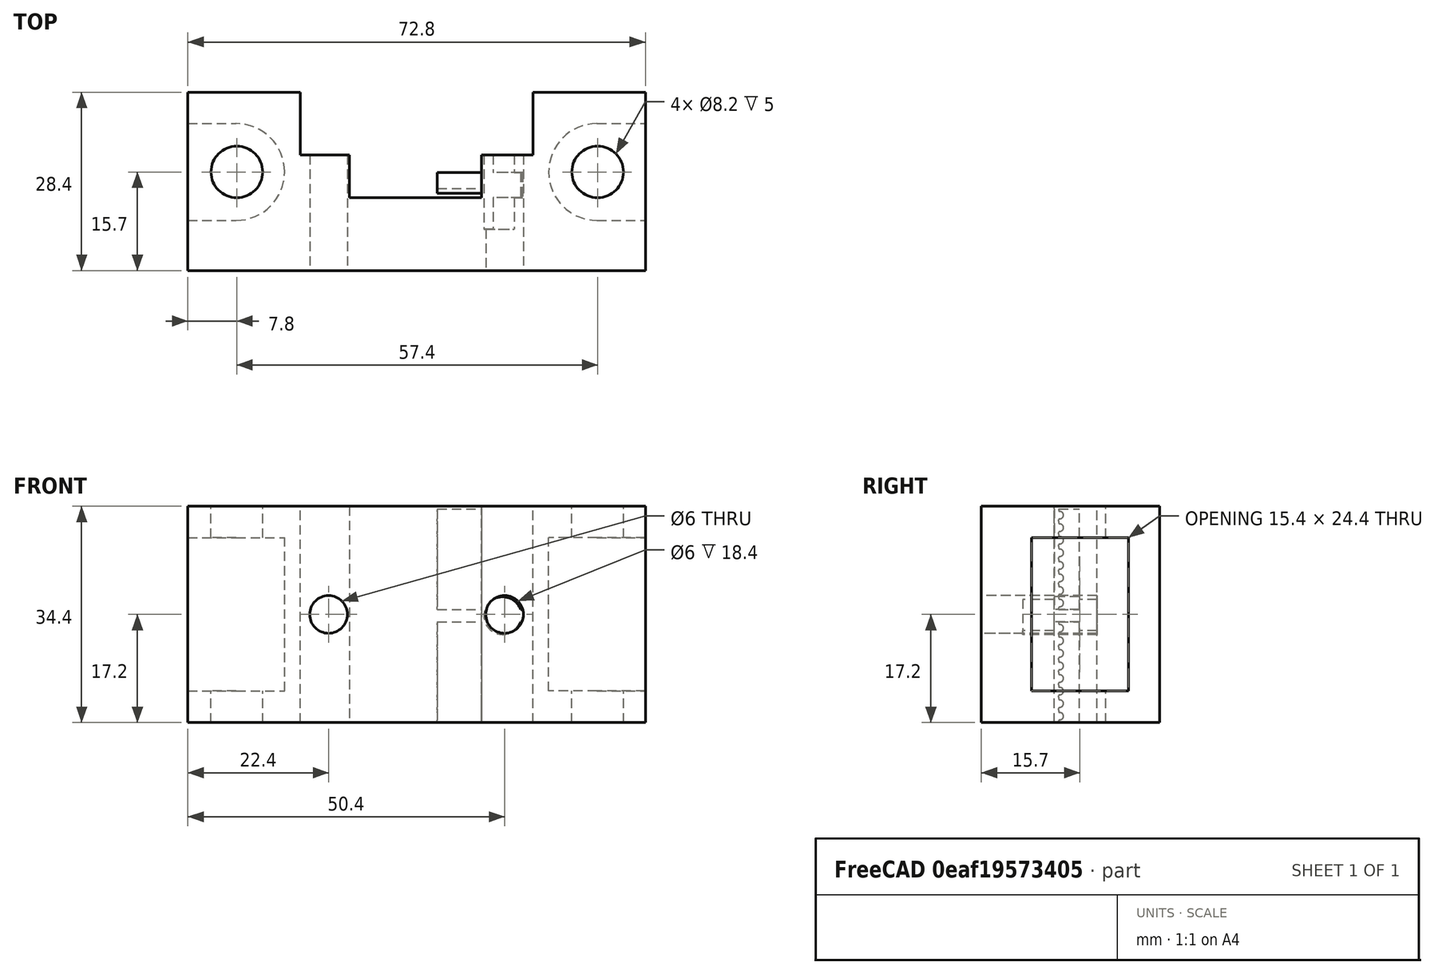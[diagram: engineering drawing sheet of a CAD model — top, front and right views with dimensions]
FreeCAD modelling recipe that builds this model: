
FCSTD DOCUMENT  (FreeCAD 0.18R16110 (Git))
Label: z-slide
License: All rights reserved
LicenseURL: http://en.wikipedia.org/wiki/All_rights_reserved
objects: Part::Cut×12, Part::Box×8, Part::Extrusion×8, Part::Cylinder×7, Part::MultiFuse×5, Spreadsheet::Sheet×2, Sketcher::SketchObject×1, Mesh::Feature×1
note: 41 computed .brp shape members not serialized (recipe doc carries the construction recipe); baked Part::Feature solids carry a one-line shape summary decoded from their .brp

FEATURE [Part::Box] Box017  label="Quader011"
  AttacherType = Attacher::AttachEngine3D
  Height = 34.4
  Length = 72.8
  Placement = pos=(1.3,-28.6,-15) rot=(0,0,1;0rad)
  Width = 3
  expr: Placement.Base.y = -Spreadsheet.z_bs - Spreadsheet.tolerance - 3
  expr: Placement.Base.x = (Spreadsheet.z_lmount - Spreadsheet.z_ls) / 2
  expr: Height = Spreadsheet.z_hs
  expr: Length = Spreadsheet.z_ls
FEATURE [Part::Cylinder] Cylinder038  label="Zylinder030"
  Angle = 360
  AttacherType = Attacher::AttachEngine3D
  Height = 25
  Placement = pos=(51.7,-5,2.2) rot=(1,0,0;1.5708rad)
  Radius = 3
  expr: Placement.Base.x = (Spreadsheet.z_lmount - Spreadsheet.z_ls) / 2 + Spreadsheet.z_ls / 2 + 14
  expr: Placement.Base.z = -15 + Spreadsheet.z_hs / 2
FEATURE [Part::Cylinder] Cylinder037  label="Zylinder029"
  Angle = 360
  AttacherType = Attacher::AttachEngine3D
  Height = 25
  Placement = pos=(23.7,-5,2.2) rot=(1,0,0;1.5708rad)
  Radius = 3
  expr: Placement.Base.x = (Spreadsheet.z_lmount - Spreadsheet.z_ls) / 2 + Spreadsheet.z_ls / 2 - 14
  expr: Placement.Base.z = -15 + Spreadsheet.z_hs / 2
FEATURE [Part::Box] Box019  label="Zahnriemen_schlitten001"
  AttacherType = Attacher::AttachEngine3D
  Height = 40
  Length = 21
  Placement = pos=(27,-17,-19) rot=(0,0,1;0rad)
  Width = 15
FEATURE [Part::Box] Box048  label="Quader027"
  AttacherType = Attacher::AttachEngine3D
  Height = 15
  Length = 16
  Width = 4
FEATURE [Part::Box] Box049  label="Quader028"
  AttacherType = Attacher::AttachEngine3D
  Height = 12
  Length = 16
  Placement = pos=(0,-4.3,-5) rot=(0,0,1;0rad)
  Width = 5
FEATURE [Part::Cylinder] Cylinder061  label="Zylinder050"
  Angle = 360
  AttacherType = Attacher::AttachEngine3D
  Height = 14
  Placement = pos=(51.4,-8,1) rot=(1,0,0;1.5708rad)
  Radius = 3
FEATURE [Part::Box] Box003  label="Quader"
  AttacherType = Attacher::AttachEngine3D
  Height = 24.4
  Length = 7.7
  Placement = pos=(-7.7,-7.7,0) rot=(0,0,1;0rad)
  Width = 15.4
  expr: Placement.Base.y = -Spreadsheet.z_dlinear / 2
  expr: Placement.Base.x = -Spreadsheet.z_dlinear / 2
  expr: Height = Spreadsheet.z_hlinear
  expr: Width = Spreadsheet.z_dlinear
  expr: Length = Spreadsheet.z_dlinear / 2
FEATURE [Part::Box] Box004  label="Quader001"
  AttacherType = Attacher::AttachEngine3D
  Height = 24.4
  Length = 7.7
  Placement = pos=(0,-7.7,0) rot=(0,0,1;0rad)
  Width = 15.4
  expr: Placement.Base.y = -Spreadsheet.z_dlinear / 2
  expr: Height = Spreadsheet.z_hlinear
  expr: Width = Spreadsheet.z_dlinear
  expr: Length = Spreadsheet.z_dlinear / 2
FEATURE [Part::Box] Box005  label="Quader002"
  AttacherType = Attacher::AttachEngine3D
  Height = 34.4
  Length = 37
  Placement = pos=(17.9,15.4,0) rot=(0,0,1;0rad)
  Width = 17
  expr: Placement.Base.y = Spreadsheet.z_bs - Spreadsheet.z_rriemepitch * 2 + 4
  expr: Placement.Base.x = Spreadsheet.z_ls / 2 - (Spreadsheet.z_lriemen + Spreadsheet.z_sriemenspiel * 2) / 2 - 2.5
  expr: Height = Spreadsheet.z_hs
  expr: Width = Spreadsheet.z_rriemepitch * 2 + 3
  expr: Length = Spreadsheet.z_lriemen + Spreadsheet.z_sriemenspiel * 2 + 5
FEATURE [Part::Box] Box  label="z_schlitten"
  AttacherType = Attacher::AttachEngine3D
  Height = 34.4
  Length = 72.8
  Width = 25.4
  expr: Length = Spreadsheet.z_ls
  expr: Height = Spreadsheet.z_hs
  expr: Width = Spreadsheet.z_bs
FEATURE [Part::Cylinder] Cylinder010  label="Zylinder006"
  Angle = 360
  AttacherType = Attacher::AttachEngine3D
  Height = 34.4
  Placement = pos=(7.8,12.7,0) rot=(0,0,1;0rad)
  Radius = 4.1
  expr: Placement.Base.y = Spreadsheet.z_bs / 2
  expr: Placement.Base.x = Spreadsheet.z_dlinear / 2 + Spreadsheet.tolerance / 2
  expr: Height = Spreadsheet.z_hs
  expr: Radius = Spreadsheet.z_df / 2 + Spreadsheet.tolerance / 2
FEATURE [Part::Cut] Cut
  Base = -> Box
  Tool = -> Cylinder010
FEATURE [Part::Cylinder] Cylinder002  label="Zylinder"
  Angle = 360
  AttacherType = Attacher::AttachEngine3D
  Height = 24.4
  Radius = 7.7
  expr: Height = Spreadsheet.z_hlinear
  expr: Radius = Spreadsheet.z_dlinear / 2
FEATURE [Part::Cylinder] Cylinder003  label="Zylinder001"
  Angle = 360
  AttacherType = Attacher::AttachEngine3D
  Height = 24.4
  Radius = 7.7
  expr: Height = Spreadsheet.z_hlinear
  expr: Radius = Spreadsheet.z_dlinear / 2
FEATURE [Part::Cylinder] Cylinder011  label="Zylinder007"
  Angle = 360
  AttacherType = Attacher::AttachEngine3D
  Height = 34.4
  Placement = pos=(65.2,12.7,0) rot=(0,0,1;0rad)
  Radius = 4.1
  expr: Placement.Base.y = Spreadsheet.z_bs / 2
  expr: Placement.Base.x = Spreadsheet.z_dlinear / 2 + Spreadsheet.z_sfa + Spreadsheet.tolerance / 2
  expr: Height = Spreadsheet.z_hs
  expr: Radius = Spreadsheet.z_df / 2 + Spreadsheet.tolerance / 2
FEATURE [Part::Cut] Cut007
  Base = -> Cut
  Tool = -> Cylinder011
FEATURE [Part::MultiFuse] Fusion001
  Placement = pos=(65.1,12.7,5) rot=(0,0,1;0rad)
  Shapes = -> [Cylinder003,Box004]
  expr: Placement.Base.z = Spreadsheet.z_swand
  expr: Placement.Base.y = Spreadsheet.z_bs / 2
  expr: Placement.Base.x = Spreadsheet.z_sfa + Spreadsheet.z_dlinear / 2
FEATURE [Part::Cut] Cut008
  Base = -> Cut007
  Tool = -> Fusion001
FEATURE [Part::MultiFuse] Fusion
  Placement = pos=(7.7,12.7,5) rot=(0,0,1;0rad)
  Shapes = -> [Box003,Cylinder002]
  expr: Placement.Base.z = Spreadsheet.z_swand
  expr: Placement.Base.y = Spreadsheet.z_bs / 2
  expr: Placement.Base.x = Spreadsheet.z_dlinear / 2
FEATURE [Part::Cut] Cut009  label="z_schlitten001"
  Base = -> Cut008
  Tool = -> Fusion
FEATURE [Part::Cut] Cut012  label="z_schlitten002"
  Base = -> Cut009
  Placement = pos=(1.3,-25.6,-15) rot=(0,0,1;0rad)
  Tool = -> Box005
  expr: Placement.Base.x = (Spreadsheet.z_lmount - Spreadsheet.z_ls) / 2
  expr: Placement.Base.y = -Spreadsheet.z_bs - Spreadsheet.tolerance
FEATURE [Part::MultiFuse] Fusion015  label="z_schlitten003"
  Shapes = -> [Box017,Cut012]
FEATURE [Part::Cut] Cut028
  Base = -> Fusion015
  Tool = -> Cylinder037
FEATURE [Part::Cut] Cut029  label="z_schlitten004"
  Base = -> Cut028
  Tool = -> Cylinder038
FEATURE [Part::Cut] Cut030  label="z_schlitten005"
  Base = -> Cut029
  Placement = pos=(0,0,-1) rot=(0,0,1;0rad)
  Tool = -> Box019
FEATURE [Spreadsheet::Sheet] Spreadsheet
  cells = A1=Toleranz; B1(tolerance)=0.2; D1=x_pos; E1=0; G1=y_pos; H1=0; A2=z_pos; B2=-10; E2=min 0 / max 297; G2=min y_pos; H2=94; I2=max 560; A3=Z-Support; D3=X-Support; G3=y-Support; J3=structure; A4=Führung d; B4(z_df)=8; D4=Führung d; E4(x_df)=10; G4=Führung d; H4(y_df)=10; J4=profil B; K4=20; A5=Führung l; B5(z_fl)==Spreadsheet.z_hub + Spreadsheet.z_hmount * 2 + Spreadsheet.z_hs - 5; D5=Führung l; E5(x_lf)=420; F5=400; G5=Führung l; H5(y_fl)=700; I5=500; J5=distanz Führung; K5=3; A6=Abstand Führung z_sfa; B6(z_sfa)==(z_dlinear + 2 * z_swand + 2 * z_sriemenspiel + z_lriemen) * 1 + (2 * x_hlinear + +z_swand - z_df + 4 * tolerance) * 0; D6=Abstand Führung x_sfa; E6(x_sfa)=65; G6=Abstand Fü y_sfa; H6(y_sfa)==x_lf - x_dlinear - 2 * y_swand; J6=höhe; K6=300; J7=add to Top; K7=18; A8=Schlittenwand swand; B8(z_swand)=5; D8=Schlitten swand; E8(x_swand)=4; G8=y_swand; H8(y_swand)=5; A9=Schlittenlänge z_ls; B9(z_ls)==z_sfa + z_dlinear; D9=Schlittenlänge; E9(x_ls)==z_lmount; A10=Schlittenbreite z_bs; B10(z_bs)==2 * z_swand + z_dlinear; D10=Schlitten breite; E10(x_bs)==Spreadsheet.x_swand * 2 + Spreadsheet.x_dlinear + Spreadsheet.x_sfa; G10=d Antrieb; H10=5; A11=Schlittenhöhe z_hs; B11(z_hs)==z_hlinear + 2 * z_swand; D11=schlittenhöhe x_hs; E11(x_hs)==x_dlinear + x_swand; A12=Hub; B12(z_hub)=100; A14=Linearlager; A15=durchmesser z_dlinear; B15(z_dlinear)=15.4; D15=durchmesser x_dlinear; E15(x_dlinear)=19.5; A16=höhe z_hlinear; B16(z_hlinear)=24.4; D16=höhe x_hlinear; E16(x_hlinear)=29.4; A18=Riemenscheibe bohrung; B18=5; A19=durchmesser z_driemen; B19(z_driemen)=16; D19=dopper pulley; E19=27.5; F19=15.8; A20=länge z_lriemen; B20(z_lriemen)=28; D20=pulley; E20=15.25; F20=15.8; G20=20 Zähne: 2* 180 °; H20=2mm*20 Zähne; I20==40mm; A21=spiel riemenscheibe z_sriemenspiel; B21(z_sriemenspiel)=2; A22=Bohreung z_dbohrung; B22(z_dbohrung)=8; C22=durchmesser Laufbuchse; D22=x_mount; A23=Bohrunlänge z_lbohrung; B23(z_lbohrung)=5; D23=Breite x_mount; E23==y_swand + x_dlinear; A24=riemenbreite z_briemen; B24(z_briemen)=6; D24=Länge x_mount; E24==x_sfa + x_df + y_swand * 2; A25=pitch z_rriemenpitch; B25(z_rriemepitch)=7; D25=Höhe x_mount; E25==y_swand * 2 + x_df + +y_swand + x_dlinear + y_swand; A26=achsen pos y; B26==-Spreadsheet.z_driemen / 2 - Spreadsheet.tolerance * 2; D26= xpos; E26==-Spreadsheet.E23; A27=achsen pos z; B27==(Spreadsheet.z_hub + Spreadsheet.z_hs + Spreadsheet.x_hs) / 2 + z_hmount - z_dbohrung / 2 - Spreadsheet.z_dbohrung / 2; D27=ypos; E27==Spreadsheet.x_swand + Spreadsheet.x_dlinear / 2 + Spreadsheet.tolerance / 2 - Spreadsheet.x_df / 2 - Spreadsheet.y_swand; D28= zpos; E28==-y_swand; A29=Mount; A30=Höhe mount; B30(z_hmount)=20; A31=Länge mount; B31(z_lmount)==z_swand * 2 + z_df + z_sfa; A32=Breite mount; B32(z_bmount)==(Spreadsheet.z_swand + Spreadsheet.z_driemen + Spreadsheet.tolerance * 2) * 0 + 26; A34=Nema; D34=Nema x; A35=Länge; B35(lnema)=42; D35(nema_x_b)=42; A36=Breite; B36(bnema)=42; D36=42; A37=Höhe; B37(hnema)=34; D37(nema_x_h)=48; A38=Achslänge; B38(lanema)=20; D38(nema_x_al)=22; A39=achsen pos y; B39(nema_achse_y)==sqrt(B43 ^ 2 - (B27 - B40) ^ 2) + B26; E39(nemax_achsey)==Spreadsheet.x_swand + Spreadsheet.x_df / 2 + Spreadsheet.x_dlinear / 2 + Spreadsheet.nema_x_h + 2; A40=achsen pos z; B40(nema_achse_z)==x_hs + lnema / 2 + 4; E40(nema_x_achsez)==-Spreadsheet.x_hs / 2; A41=achsen pos x; B41(nema_achse_x)==(z_lmount - z_lriemen) / 2 - z_sriemenspiel; E41(nema_x_achsex)==Spreadsheet.x_lf - Spreadsheet.nema_x_b / 2 - Spreadsheet.y_df; A42=länge zahnriemen; B42=200; C42=gerechnet; A43=abstand achsen; B43==(B42 - 40) / 2; C43==sqrt((Spreadsheet.B27 - Spreadsheet.nema_achse_z) ^ 2 + (-Spreadsheet.B26 + Spreadsheet.nema_achse_y) ^ 2) * 2 + 2 * pi * 7; D43=Zahnriemen x; D44=Breite; E44=6; A45=doppel pulley; D45=Höhe; E45==(Spreadsheet.F20 + Spreadsheet.tolerance * 2) * 0 + 15; A46= achse1  x pos; B46==z_lmount / 2 - (6.5 + 8.9) / 2; D46=Länge; E46==y_sfa + x_dlinear + y_swand * 2 + 2 + nema_x_b / 2; A47= achse2 xpos; B47==z_lmount / 2 + (6.5 + 8.9) / 2; B48==-atan((Spreadsheet.B27 - Spreadsheet.nema_achse_z) / (-Spreadsheet.B26 + Spreadsheet.nema_achse_y))
FEATURE [Sketcher::SketchObject] Sketch
  MapMode = 2
  Placement = pos=(0,0,0) rot=(0,1,0;3.14159rad)
  expr: Constraints[11] = Spreadsheet001.B5
  expr: Constraints[30] = Spreadsheet001.B1 / 2
  expr: Constraints[25] = Spreadsheet001.B2 - Spreadsheet001.B3
  expr: Constraints[16] = Spreadsheet001.B2 - Spreadsheet001.B3
  expr: Constraints[18] = Spreadsheet001.B6
  expr: Constraints[36] = Spreadsheet001.B6
  expr: Constraints[33] = Spreadsheet001.B2 - Spreadsheet001.B3
  expr: Constraints[17] = Spreadsheet001.B1 / 2
  expr: Constraints[9] = Spreadsheet001.B2 - Spreadsheet001.B3
  expr: Constraints[2] = Spreadsheet001.B2 - Spreadsheet001.B4
  sketch-geometry (16):
    g0: LineSegment [constr] StartX=0 StartY=0 StartZ=0 EndX=0 EndY=-0.825 EndZ=0
    g1: ArcOfCircle CenterX=0 CenterY=-0.825 CenterZ=0 NormalX=0 NormalY=0 NormalZ=1 AngleXU=0 Radius=0.555 StartAngle=3.59519 EndAngle=5.82959
    g2: LineSegment [constr] StartX=0 StartY=0 StartZ=0 EndX=0.4 EndY=0 EndZ=0
    g3: LineSegment [constr] StartX=0.4 StartY=0 StartZ=0 EndX=0.4 EndY=-0.63 EndZ=0
    g4: ArcOfCircle CenterX=0.4 CenterY=-0.63 CenterZ=0 NormalX=0 NormalY=0 NormalZ=1 AngleXU=0 Radius=1 StartAngle=3.2724 EndAngle=3.59519
    g5: LineSegment StartX=0 StartY=0 StartZ=0 EndX=-1 EndY=0 EndZ=0
    g6: LineSegment StartX=-1 StartY=0 StartZ=0 EndX=-1 EndY=-0.63 EndZ=0
    g7: ArcOfCircle CenterX=-0.740175 CenterY=-0.78 CenterZ=0 NormalX=0 NormalY=0 NormalZ=1 AngleXU=0 Radius=0.15 StartAngle=0.130807 EndAngle=1.5708
    g8: LineSegment StartX=-1 StartY=-0.63 StartZ=0 EndX=-0.740175 EndY=-0.63 EndZ=0
    g9: LineSegment [constr] StartX=0 StartY=0 StartZ=0 EndX=-0.4 EndY=0 EndZ=0
    g10: LineSegment [constr] StartX=-0.4 StartY=0 StartZ=0 EndX=-0.4 EndY=-0.63 EndZ=0
    g11: ArcOfCircle CenterX=-0.4 CenterY=-0.63 CenterZ=0 NormalX=0 NormalY=0 NormalZ=1 AngleXU=0 Radius=1 StartAngle=5.82959 EndAngle=6.15238
    g12: LineSegment StartX=0 StartY=0 StartZ=0 EndX=1 EndY=0 EndZ=0
    g13: LineSegment StartX=1 StartY=0 StartZ=0 EndX=1 EndY=-0.63 EndZ=0
    g14: LineSegment StartX=1 StartY=-0.63 StartZ=0 EndX=0.740175 EndY=-0.63 EndZ=0
    g15: ArcOfCircle CenterX=0.740175 CenterY=-0.78 CenterZ=0 NormalX=0 NormalY=0 NormalZ=1 AngleXU=0 Radius=0.15 StartAngle=1.5708 EndAngle=3.01079
  constraints (43):
    c: Coincident(g0,g-1)
    c: Vertical(g0)
    c: DistanceY(g0,g0) = 0.825
    c: Coincident(g1,g0)
    c: Coincident(g2,g-1)
    c: Horizontal(g2)
    c: DistanceX(g2,g2) = 0.4
    c: Coincident(g3,g2)
    c: Vertical(g3)
    c: DistanceY(g3,g3) = 0.63
    c: Coincident(g4,g3)
    c: Radius(g4) = 1
    c: Coincident(g5,g-1)
    c: Horizontal(g5)
    c: Coincident(g6,g5)
    c: Vertical(g6)
    c: DistanceY(g6,g6) = 0.63
    c: DistanceX(g5,g5) = 1
    c: Radius(g7) = 0.15
    c: Coincident(g8,g6)
    c: Horizontal(g8)
    c: Coincident(g9,g-1)
    c: Distance(g9) = 0.4
    c: Coincident(g10,g9)
    c: Vertical(g10)
    c: DistanceY(g10,g10) = 0.63
    c: Horizontal(g9)
    c: Coincident(g11,g10)
    c: Coincident(g12,g-1)
    c: Horizontal(g12)
    c: DistanceX(g12,g12) = 1
    c: Coincident(g13,g12)
    c: Vertical(g13)
    c: DistanceY(g13,g13) = 0.63
    c: Coincident(g14,g13)
    c: Horizontal(g14)
    c: Radius(g15) = 0.15
    c: Tangent(g15,g14) = -1.5708
    c: Tangent(g7,g8) = 1.5708
    c: Tangent(g7,g4) = 1.5708
    c: Tangent(g15,g11) = 1.5708
    c: Tangent(g4,g1) = -1.5708
    c: Tangent(g11,g1) = -1.5708
FEATURE [Part::Extrusion] Extrude001
  Base = -> Sketch
  Dir = (0,0,-1)
  DirMode = 2
  FaceMakerClass = Part::FaceMakerBullseye
  LengthFwd = 7
  LengthRev = 0
  Placement = pos=(2,0,0) rot=(0,0,1;0rad)
  Solid = true
  Symmetric = false
FEATURE [Part::Extrusion] Extrude003
  Base = -> Sketch
  Dir = (0,0,-1)
  DirMode = 2
  FaceMakerClass = Part::FaceMakerBullseye
  LengthFwd = 7
  LengthRev = 0
  Placement = pos=(6,0,0) rot=(0,0,1;0rad)
  Solid = true
  Symmetric = false
FEATURE [Part::Extrusion] Extrude004
  Base = -> Sketch
  Dir = (0,0,-1)
  DirMode = 2
  FaceMakerClass = Part::FaceMakerBullseye
  LengthFwd = 7
  LengthRev = 0
  Placement = pos=(10,0,0) rot=(0,0,1;0rad)
  Solid = true
  Symmetric = false
FEATURE [Part::Extrusion] Extrude
  Base = -> Sketch
  Dir = (0,0,-1)
  DirMode = 2
  FaceMakerClass = Part::FaceMakerBullseye
  LengthFwd = 7
  LengthRev = 0
  Solid = true
  Symmetric = false
FEATURE [Part::Extrusion] Extrude007
  Base = -> Sketch
  Dir = (0,0,-1)
  DirMode = 2
  FaceMakerClass = Part::FaceMakerBullseye
  LengthFwd = 7
  LengthRev = 0
  Placement = pos=(12,0,0) rot=(0,0,1;0rad)
  Solid = true
  Symmetric = false
FEATURE [Part::Extrusion] Extrude002
  Base = -> Sketch
  Dir = (0,0,-1)
  DirMode = 2
  FaceMakerClass = Part::FaceMakerBullseye
  LengthFwd = 7
  LengthRev = 0
  Placement = pos=(4,0,0) rot=(0,0,1;0rad)
  Solid = true
  Symmetric = false
FEATURE [Part::Extrusion] Extrude005
  Base = -> Sketch
  Dir = (0,0,-1)
  DirMode = 2
  FaceMakerClass = Part::FaceMakerBullseye
  LengthFwd = 7
  LengthRev = 0
  Placement = pos=(8,0,0) rot=(0,0,1;0rad)
  Solid = true
  Symmetric = false
FEATURE [Part::Extrusion] Extrude006
  Base = -> Sketch
  Dir = (0,0,-1)
  DirMode = 2
  FaceMakerClass = Part::FaceMakerBullseye
  LengthFwd = 7
  LengthRev = 0
  Placement = pos=(14,0,0) rot=(0,0,1;0rad)
  Solid = true
  Symmetric = false
FEATURE [Part::MultiFuse] Fusion030  label="Form Zahnriemen"
  Placement = pos=(15,0.1,7) rot=(0,0,1;3.14159rad)
  Shapes = -> [Extrude005,Extrude002,Extrude003,Extrude,Extrude001,Extrude004,Extrude007,Extrude006]
FEATURE [Part::Cut] Cut059
  Base = -> Box048
  Tool = -> Fusion030
FEATURE [Part::Cut] Cut066  label="Zahnriemen Befestigung006"
  Base = -> Cut059
  Placement = pos=(41,-17,0) rot=(0,1,0;1.5708rad)
  Tool = -> Box049
  expr: Placement.Base.x = +41
FEATURE [Part::Cut] Cut067  label="Zahnriemen Befestigung007"
  Base = -> Cut059
  Placement = pos=(41,-17,18) rot=(0,1,0;1.5708rad)
  Tool = -> Box049
  expr: Placement.Base.x = 41
FEATURE [Part::MultiFuse] Fusion034
  Shapes = -> [Cut030,Cut066,Cut067]
FEATURE [Part::Cut] Cut068  label="z-slide"
  Base = -> Fusion034
  Placement = pos=(0,0,-10) rot=(0,0,1;0rad)
  Tool = -> Cylinder061
  expr: Placement.Base.x = Spreadsheet.E1
  expr: Placement.Base.y = Spreadsheet.H1
  expr: Placement.Base.z = Spreadsheet.B2
FEATURE [Spreadsheet::Sheet] Spreadsheet001
  cells = A1=abstand zähne; B1=2; A2=dicke; B2=1.38; A3=zahntiefe; B3=0.75; A4=r1; B4=0.555; A5=r2; B5=1; A6=r3; B6=0.15; A7=pitch; B7=0.254; A8=tolerance; B8=0.1
FEATURE [Mesh::Feature] Mesh  label="z-slide (Meshed)"
